# Revit family: Grid_Drain-DXV-Modulus-D35120460_Series
name_source: partatom
category: Plumbing Fixtures
revit_build: Autodesk Revit 2018 (Build: 20170223_1515(x64)
units: mm (PartAtom-declared; Revit-internal decimal feet)

## family parameters
Cut with Voids When Loaded = No
Host = Face
OmniClass Number = 23.70.50.21.24
OmniClass Title = Waste Water Drains
Part Type = Normal
Room Calculation Point = No
Round Connector Dimension = Use Diameter
Shared = Yes

## types (4) — shared parameters
Assembly Code = D2030300
CW Connection = No
Default Elevation = 0"
Description = DXV Modulus Grid Drain
HW Connection = No
Installation Type = Floor Mounted
Length = 7 11/16"
Manufacturer = DXV
Price = Prices may vary. Please consult Manufacturer Representative for most up-to-date price list.
Product Documentation Link = https://dxv01.blob.core.windows.net
Product Page URL = https://www.dxv.com
Revised Date = 04/05/2021
URL = https://www.dxv.com
Vent Connection = No
Waste Connection = Yes
Waste Connection Diameter = 1 1/4"
Width = 2 3/8"
zero-valued in all types: CWFU, HWFU, WFU

## per-type parameters (varying)
| type | Finish | Material |
| D35120460.100 | Metal-DXV-100-Polished_Chrome | Metal-DXV-100-Polished_Chrome |
| D35120460.144 | Metal-DXV-144-Brushed_Nickel | Metal-DXV-144-Brushed_Nickel |
| D35120460.150 | Metal-DXV-150-Platinum_Nickel | Metal-DXV-150-Platinum_Nickel |
| D35120460.243 | Metal-DXV-243-Matte_Black | Metal-DXV-243-Matte_Black |

note: column(s) folded — value = type name in every type: Model

## geometry (parser evidence)
native form markers: Sweep x2
no freeform markers — native parametric forms only
